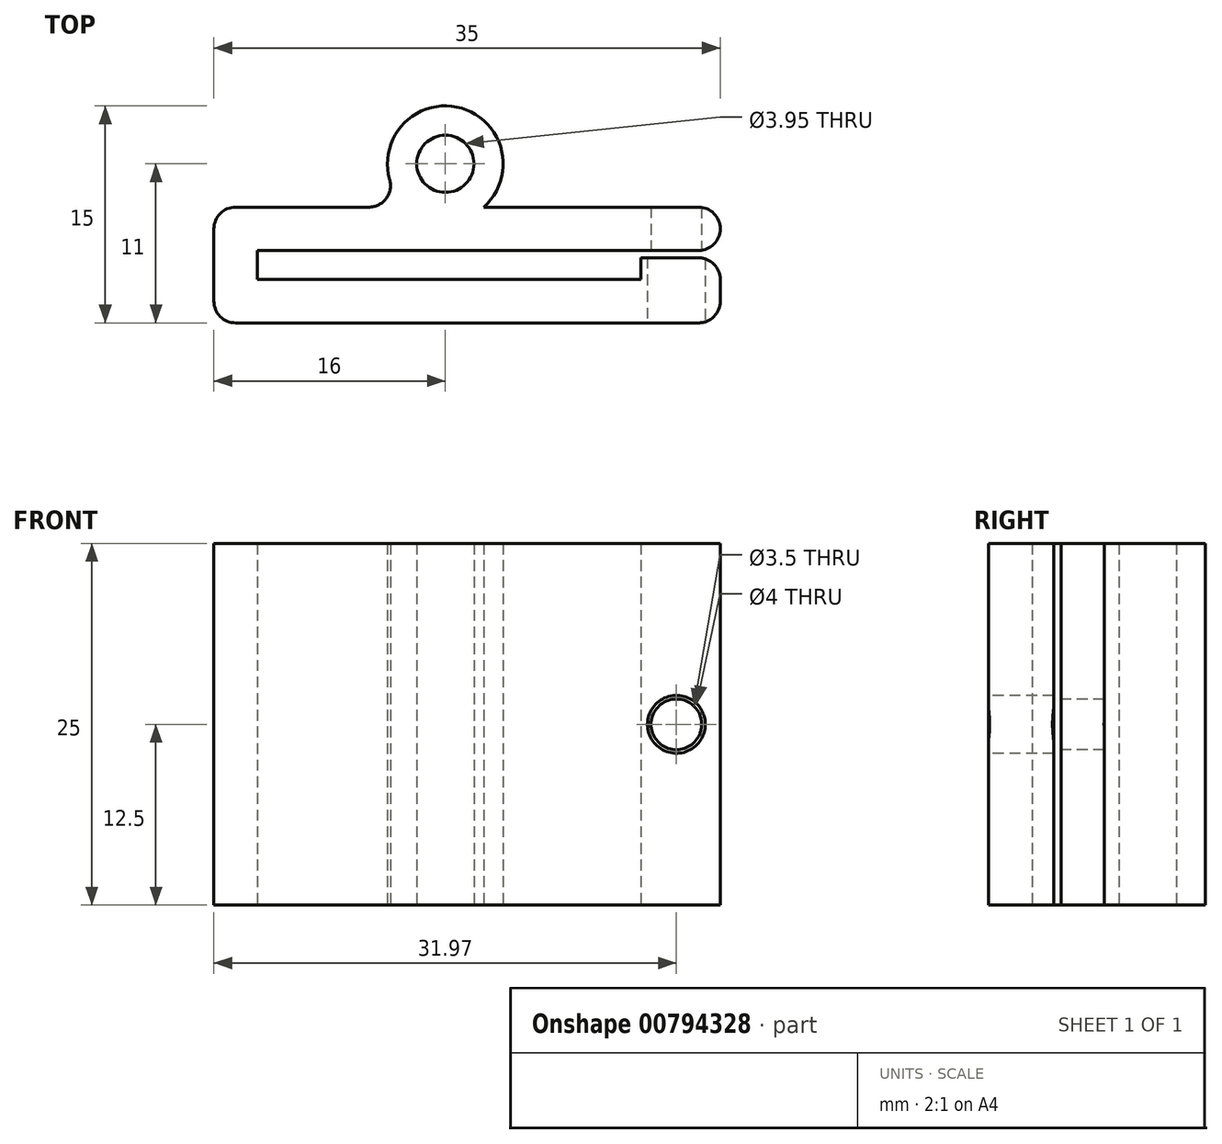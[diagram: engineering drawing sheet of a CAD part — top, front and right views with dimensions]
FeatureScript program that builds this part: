
annotation { "Feature Type Name" : "Feature", "Feature Type Description" : "" }
export const myFeature = defineFeature(function(context is Context, id is Id, definition is map)
    precondition{}
    {
        {
            var Q0;
            Q0=qCreatedBy(makeId("Top.planeOp"),FACE);
            var sketch = newSketch(context, id + "F0", { "sketchPlane" : qUnion([Q0])});
            skCircle(sketch, "E0", {"center": v(0, 11) * mm, "radius": 1.98 * mm});
            skArc(sketch, "E1", {"start": v(2.65, 8) * mm, "mid": v(0, 15) * mm, "end": v(-2.65, 8) * mm});
            skLineSegment(sketch, "E2.bottom", {"start": v(-16, 0) * mm, "end": v(19, 0) * mm});
            skLineSegment(sketch, "E2.top", {"start": v(-16, 8) * mm, "end": v(-2.65, 8) * mm});
            skLineSegment(sketch, "E2.left", {"start": v(-16, 0) * mm, "end": v(-16, 8) * mm});
            skLineSegment(sketch, "E2.right", {"start": v(19, 0) * mm, "end": v(19, 3) * mm});
            skLineSegment(sketch, "E3.bottom", {"start": v(19, 5) * mm, "end": v(-13, 5) * mm});
            skLineSegment(sketch, "E3.top", {"start": v(19, 3) * mm, "end": v(-13, 3) * mm});
            skLineSegment(sketch, "E3.right", {"start": v(-13, 5) * mm, "end": v(-13, 3) * mm});
            skLineSegment(sketch, "E4.trimOffspring", {"start": v(19, 5) * mm, "end": v(19, 8) * mm});
            skLineSegment(sketch, "E5", {"start": v(17.2, 3) * mm, "end": v(19, 3) * mm});
            skLineSegment(sketch, "E6.trimOffspring", {"start": v(2.65, 8) * mm, "end": v(19, 8) * mm});
            skLineSegment(sketch, "E7.bottom", {"start": v(19, 3) * mm, "end": v(13.5, 3) * mm});
            skLineSegment(sketch, "E7.top", {"start": v(19, 4.5) * mm, "end": v(13.5, 4.5) * mm});
            skLineSegment(sketch, "E7.left", {"start": v(19, 3) * mm, "end": v(19, 4.5) * mm});
            skLineSegment(sketch, "E7.right", {"start": v(13.5, 3) * mm, "end": v(13.5, 4.5) * mm});
            skSolve(sketch);
        }
        {
            var Q0;
            Q0=makeQuery(id+"F0.imprint","IMPRINT",FACE,{"disambiguationData":[TD([[makeQuery(id+"F0.imprint","IMPRINT",EDGE,{"derivedFrom":sQuery(id+"F0.wireOp",EDGE,"E0")}),-1.0]])]});
            var Q1;
            {var subQ0=sQuery(id+"F0.wireOp",EDGE,"E2.top");var subQ1=sQuery(id+"F0.wireOp",EDGE,"E1");var subQ2=makeQuery(id+"F0.imprint","INTERSECT",VERTEX,{"disambiguationData":[OD(0.0)],"derivedFrom":[subQ1,subQ0]});Q1=makeQuery(id+"F0.imprint","IMPRINT",FACE,{"disambiguationData":[TD([[makeQuery(id+"F0.imprint","IMPRINT",EDGE,{"disambiguationData":[TD([[subQ2,-1.0]])],"derivedFrom":subQ1}),1.0]])]});}
            var Q2;
            Q2=makeQuery(id+"F0.imprint","IMPRINT",FACE,{"disambiguationData":[TD([[makeQuery(id+"F0.imprint","IMPRINT",EDGE,{"derivedFrom":sQuery(id+"F0.wireOp",EDGE,"E2.bottom")}),1.0]])]});
            var Q3;
            {var subQ0=sQuery(id+"F0.wireOp",EDGE,"T43YfDp4-rqTj-D4gC-lWhI-xTIGRzKKKMs4");var subQ1=sQuery(id+"F0.wireOp",EDGE,"E3.top");var subQ3=makeQuery(id+"F0.imprint","INTERSECT",VERTEX,{"derivedFrom":[subQ1,subQ0]});Q3=makeQuery(id+"F0.imprint","IMPRINT",FACE,{"disambiguationData":[TD([[makeQuery(id+"F0.imprint","IMPRINT",EDGE,{"disambiguationData":[TD([[subQ3,1.0]])],"derivedFrom":subQ1}),1.0]])]});}
            var Q4;
            {var subQ0=sQuery(id+"F0.wireOp",EDGE,"T43YfDp4-rqTj-D4gC-lWhI-xTIGRzKKKMs4");var subQ4=makeQuery(id+"F0.imprint","INTERSECT",VERTEX,{"derivedFrom":[subQ0,sQuery(id+"F0.wireOp",EDGE,"PRyrmNaC-yeQ7-V4HT-Spjw-x5LiDcZg38KU")]});Q4=makeQuery(id+"F0.imprint","IMPRINT",FACE,{"disambiguationData":[TD([[makeQuery(id+"F0.imprint","IMPRINT",EDGE,{"disambiguationData":[TD([[subQ4,-1.0]])],"derivedFrom":subQ0}),1.0]])]});}
            var Q5;
            {var subQ0=sQuery(id+"F0.wireOp",EDGE,"PRyrmNaC-yeQ7-V4HT-Spjw-x5LiDcZg38KU");var subQ1=sQuery(id+"F0.wireOp",EDGE,"E3.bottom");var subQ3=makeQuery(id+"F0.imprint","INTERSECT",VERTEX,{"derivedFrom":[subQ1,subQ0]});Q5=makeQuery(id+"F0.imprint","IMPRINT",FACE,{"disambiguationData":[TD([[makeQuery(id+"F0.imprint","IMPRINT",EDGE,{"disambiguationData":[TD([[subQ3,1.0]])],"derivedFrom":subQ1}),-1.0]])]});}
            var Q6;
            Q6=makeQuery(id+"F0.imprint","IMPRINT",FACE,{"disambiguationData":[TD([[makeQuery(id+"F0.imprint","IMPRINT",EDGE,{"derivedFrom":sQuery(id+"F0.wireOp",EDGE,"XuVYnssw-9Ml2-bUPo-iZA2-qH8SVfEcoueC")}),1.0]])]});
            var Q7;
            Q7=makeQuery(id+"F0.imprint","IMPRINT",FACE,{"disambiguationData":[TD([[makeQuery(id+"F0.imprint","IMPRINT",EDGE,{"derivedFrom":sQuery(id+"F0.wireOp",EDGE,"E7.top")}),1.0]])]});
            extrude(context, id + "F1", {"entities" : qUnion([Q0, Q1, Q2, Q3, Q4, Q5, Q6, Q7]), "depth" : 25 * mm, "offsetDistance" : 25 * mm});
        }
        {
            var Q0;
            Q0=makeQuery(id+"F1.opExtrude","SWEPT_EDGE",EDGE,{"disambiguationData":[OSD([sQuery(id+"F0.wireOp",EDGE,"E2.top"),sQuery(id+"F0.wireOp",EDGE,"E2.left")])]});
            var Q1;
            Q1=makeQuery(id+"F1.opExtrude","SWEPT_EDGE",EDGE,{"disambiguationData":[OSD([sQuery(id+"F0.wireOp",EDGE,"E2.bottom"),sQuery(id+"F0.wireOp",EDGE,"E2.left")])]});
            var Q2;
            Q2=makeQuery(id+"F1.opExtrude","SWEPT_EDGE",EDGE,{"disambiguationData":[OSD([sQuery(id+"F0.wireOp",EDGE,"E2.bottom"),sQuery(id+"F0.wireOp",EDGE,"E2.right")])]});
            var Q3;
            Q3=makeQuery(id+"F1.opExtrude","SWEPT_EDGE",EDGE,{"disambiguationData":[OSD([sQuery(id+"F0.wireOp",EDGE,"E2.top"),sQuery(id+"F0.wireOp",EDGE,"E4.trimOffspring")])]});
            var Q4;
            Q4=makeQuery(id+"F1.opExtrude","SWEPT_EDGE",EDGE,{"disambiguationData":[OSD([sQuery(id+"F0.wireOp",EDGE,"E3.bottom"),sQuery(id+"F0.wireOp",EDGE,"E4.trimOffspring")])]});
            var Q5;
            Q5=makeQuery(id+"F1.opExtrude","SWEPT_EDGE",EDGE,{"disambiguationData":[OSD([sQuery(id+"F0.wireOp",EDGE,"E7.top"),sQuery(id+"F0.wireOp",EDGE,"E7.left")])]});
            fillet(context, id + "F2", {"entities" : qUnion([Q0, Q1, Q2, Q3, Q4, Q5]), "radius" : 1.5 * mm, "tangentPropagation" : true, "allowEdgeOverflow" : false});
        }
        {
            var Q0;
            Q0=makeQuery(id+"F1.opExtrude","SWEPT_FACE",FACE,{"disambiguationData":[OSD([sQuery(id+"F0.wireOp",EDGE,"E2.bottom")])]});
            var sketch = newSketch(context, id + "F3", { "sketchPlane" : qUnion([Q0])});
            skCircle(sketch, "E8", {"center": v(15.97, 12.5) * mm, "radius": 2 * mm});
            skPoint(sketch, "E8.centerSnap0", {"position": v(17.5, 12.5) * mm});
            skCircle(sketch, "E9", {"center": v(15.97, 12.5) * mm, "radius": 1.75 * mm});
            skSolve(sketch);
        }
        {
            var Q0;
            {var subQ0=sQuery(id+"F3.wireOp",EDGE,"E9");var subQ1=sQuery(id+"F0.wireOp",EDGE,"E2.bottom");var subQ2=makeQuery(id+"F2.opFillet","BLEND_EDGE",EDGE,{"blendedFrom":[makeQuery(id+"F1.opExtrude","SWEPT_EDGE",EDGE,{"disambiguationData":[OSD([subQ1,sQuery(id+"F0.wireOp",EDGE,"E2.right")])]}),makeQuery(id+"F1.opExtrude","SWEPT_FACE",FACE,{"disambiguationData":[OSD([subQ1])]})],"blendedInto":[makeQuery(id+"F1.opExtrude","SWEPT_FACE",FACE,{"disambiguationData":[OSD([subQ1])]})]});var subQ3=makeQuery(id+"F3.imprint","INTERSECT",VERTEX,{"disambiguationData":[OD(0.0)],"derivedFrom":[subQ2,subQ0]});Q0=makeQuery(id+"F3.imprint","IMPRINT",FACE,{"disambiguationData":[TD([[makeQuery(id+"F3.imprint","IMPRINT",EDGE,{"disambiguationData":[TD([[subQ3,1.0]])],"derivedFrom":subQ0}),1.0]])]});}
            var Q1;
            {var subQ0=sQuery(id+"F3.wireOp",EDGE,"E9");var subQ1=sQuery(id+"F0.wireOp",EDGE,"E2.bottom");var subQ2=makeQuery(id+"F2.opFillet","BLEND_EDGE",EDGE,{"blendedFrom":[makeQuery(id+"F1.opExtrude","SWEPT_EDGE",EDGE,{"disambiguationData":[OSD([subQ1,sQuery(id+"F0.wireOp",EDGE,"E2.right")])]}),makeQuery(id+"F1.opExtrude","SWEPT_FACE",FACE,{"disambiguationData":[OSD([subQ1])]})],"blendedInto":[makeQuery(id+"F1.opExtrude","SWEPT_FACE",FACE,{"disambiguationData":[OSD([subQ1])]})]});var subQ3=makeQuery(id+"F3.imprint","INTERSECT",VERTEX,{"disambiguationData":[OD(0.0)],"derivedFrom":[subQ2,subQ0]});Q1=makeQuery(id+"F3.imprint","IMPRINT",FACE,{"disambiguationData":[TD([[makeQuery(id+"F3.imprint","IMPRINT",EDGE,{"disambiguationData":[TD([[subQ3,-1.0]])],"derivedFrom":subQ0}),1.0]])]});}
            extrude(context, id + "F4", {"entities" : qUnion([Q0, Q1]), "operationType" : NewBodyOperationType.REMOVE, "oppositeDirection" : true, "depth" : 25 * mm, "offsetDistance" : 25 * mm});
        }
        {
            var Q0;
            {var subQ0=sQuery(id+"F3.wireOp",EDGE,"E8");var subQ1=sQuery(id+"F0.wireOp",EDGE,"E2.bottom");var subQ2=makeQuery(id+"F2.opFillet","BLEND_EDGE",EDGE,{"blendedFrom":[makeQuery(id+"F1.opExtrude","SWEPT_EDGE",EDGE,{"disambiguationData":[OSD([subQ1,sQuery(id+"F0.wireOp",EDGE,"E2.right")])]}),makeQuery(id+"F1.opExtrude","SWEPT_FACE",FACE,{"disambiguationData":[OSD([subQ1])]})],"blendedInto":[makeQuery(id+"F1.opExtrude","SWEPT_FACE",FACE,{"disambiguationData":[OSD([subQ1])]})]});var subQ3=makeQuery(id+"F3.imprint","INTERSECT",VERTEX,{"disambiguationData":[OD(0.0)],"derivedFrom":[subQ2,subQ0]});Q0=makeQuery(id+"F3.imprint","IMPRINT",FACE,{"disambiguationData":[TD([[makeQuery(id+"F3.imprint","IMPRINT",EDGE,{"disambiguationData":[TD([[subQ3,1.0]])],"derivedFrom":subQ0}),1.0]])]});}
            var Q1;
            {var subQ0=sQuery(id+"F3.wireOp",EDGE,"E8");var subQ1=sQuery(id+"F0.wireOp",EDGE,"E2.bottom");var subQ2=makeQuery(id+"F2.opFillet","BLEND_EDGE",EDGE,{"blendedFrom":[makeQuery(id+"F1.opExtrude","SWEPT_EDGE",EDGE,{"disambiguationData":[OSD([subQ1,sQuery(id+"F0.wireOp",EDGE,"E2.right")])]}),makeQuery(id+"F1.opExtrude","SWEPT_FACE",FACE,{"disambiguationData":[OSD([subQ1])]})],"blendedInto":[makeQuery(id+"F1.opExtrude","SWEPT_FACE",FACE,{"disambiguationData":[OSD([subQ1])]})]});var subQ3=makeQuery(id+"F3.imprint","INTERSECT",VERTEX,{"disambiguationData":[OD(0.0)],"derivedFrom":[subQ2,subQ0]});Q1=makeQuery(id+"F3.imprint","IMPRINT",FACE,{"disambiguationData":[TD([[makeQuery(id+"F3.imprint","IMPRINT",EDGE,{"disambiguationData":[TD([[subQ3,-1.0]])],"derivedFrom":subQ0}),1.0]])]});}
            extrude(context, id + "F5", {"entities" : qUnion([Q0, Q1]), "operationType" : NewBodyOperationType.REMOVE, "oppositeDirection" : true, "depth" : 4.8 * mm, "offsetDistance" : 25 * mm});
        }
    });
